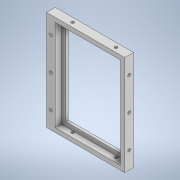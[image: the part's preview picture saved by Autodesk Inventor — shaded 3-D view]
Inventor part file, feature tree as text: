
AUTODESK INVENTOR PART (.ipt)
format: ipt  version: 2022.2 (Build 262287030, 287C)  size: 171,520 bytes
history: native  units: in
note: dims shown in document units (in); Inventor stores cm internally (conversion verified against a paired STEP export)
features: sketch x7, hole x4, extrude x3
ambient origin geometry x8: Origin, YZ Plane, XZ Plane, XY Plane, X Axis, Y Axis, Z Axis, Center Point
bodies: Solid1 (feature_tree)
feature tree (14):
  extrude  "Extrusion1"  Depth=4.5276in
  hole  "Hole1"  [1 undecoded]
  hole  "Hole2"  [1 undecoded]
  hole  "Hole3"  [1 undecoded]
  hole  "Hole4"  [1 undecoded]
  extrude  "Extrusion2"  Depth=0.1969in
  extrude  "Extrusion3"  Depth=0.3937in
  sketch  "Sketch1"  dims[d0=3.5433in d1=4.5276in]
  sketch  "Sketch2"  dims[d2=0.3937in d3=0.0in d4=0.7874in]
  sketch  "Sketch3"  dims[d5=0.1969in d6=1.1811in d8=1.4764in d9=0.3937in d11=0.3937in]
  sketch  "Sketch4"  dims[d13=0.125in d14=0.2953in d15=0.1476in d16=0.0984in d17=90.0deg d18=0.1969in d19=0.0in d20=0.9843in]
  sketch  "Sketch5"  dims[d21=0.1969in d22=0.7874in d24=1.9685in d25=0.3937in d27=0.3937in]
  sketch  "Sketch6"  dims[d29=0.125in d30=0.2953in d31=0.1476in d32=0.0984in d33=90.0deg d34=0.1969in d35=0.0in d36=0.9843in]
  sketch  "Sketch7"  dims[d37=0.1969in d38=0.7874in d40=1.9685in d41=0.3937in d43=0.3937in d45=0.125in d46=0.2953in d47=0.1476in d48=0.0984in d49=90.0deg d50=0.1969in d51=0.0in d52=0.1969in d53=0.7874in d54=1.1811in d56=1.4764in d57=0.3937in d59=0.3937in d61=0.125in d62=0.2953in d63=0.1476in d64=0.0984in d65=90.0deg d66=0.1969in d67=0.0in d68=0.3937in d69=0.1969in d72=0.1969in d74=0.1969in d75=0.2756in d76=0.0in d77=0.1969in d78=0.1969in d79=0.1969in d81=0.1969in d82=0.0in d83=0.0in]
note: 4 required parameter values undecoded (feature->parameter linkage not recoverable at this tier; creation-order binding heuristic only, values carry confidence <= 0.55)
